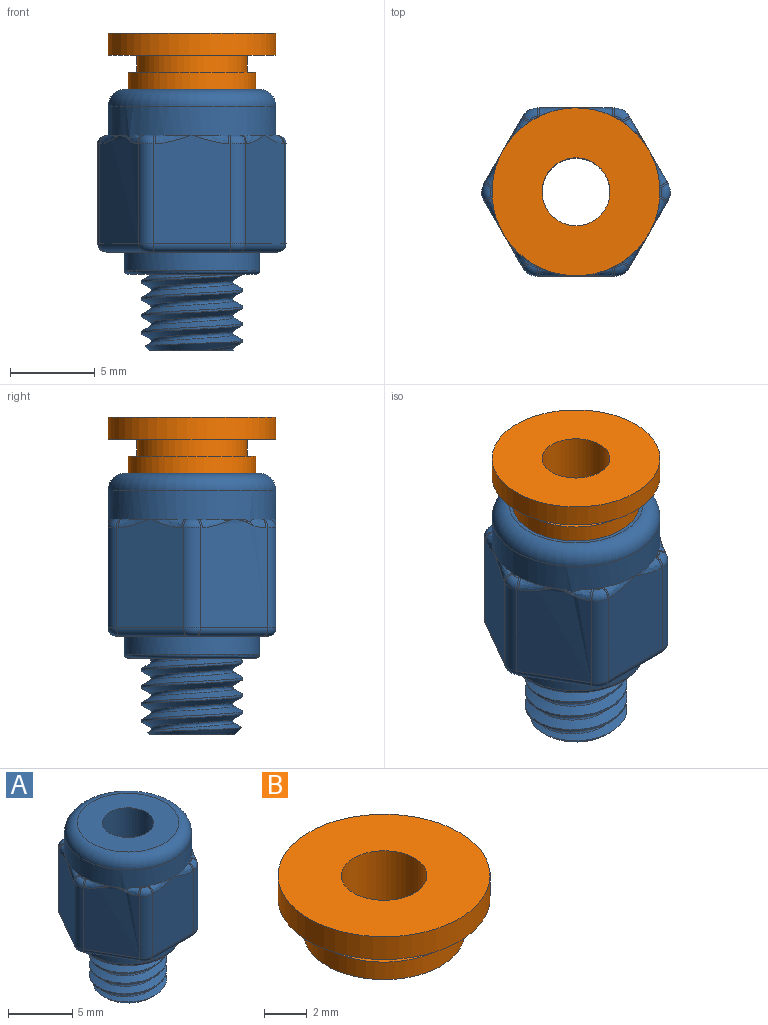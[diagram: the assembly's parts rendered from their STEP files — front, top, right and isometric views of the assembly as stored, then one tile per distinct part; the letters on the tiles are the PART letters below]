
ASSEMBLY  parts=2 mates=1
PART A: 76 faces, bbox 11.7x11.1x16.2 mm
  f0: plane 0.6x0.35mm, normal (0,0,1), area 0.1mm2, adj f1,f73,f74,f75
  f1: cylinder r=0.5mm len=0.5mm, axis (0.5,-0.87,0), area 0.1mm2, adj f0,f2,f72,f75
  f2: plane 6.78x4.33mm, normal (0.87,0.5,0), area 27.7mm2, adj f1,f3,f67,f68,f69,f70,f71,f72
  f3: cylinder r=0.5mm len=0.5mm, axis (0.5,-0.87,0), area 0.1mm2, adj f2,f4,f66,f68
  f4: plane 0.7x0.12mm, normal (0,0,1), area 0.1mm2, adj f3,f5,f66,f73
  f5: cylinder r=0.5mm len=0.5mm, axis (-0.5,-0.87,0), area 0.1mm2, adj f4,f6,f65,f66
  f6: plane 6.4x3.95mm, normal (0.87,-0.5,0), area 27.7mm2, adj f5,f7,f62,f63,f64,f65,f71
  f7: cylinder r=0.5mm len=0.5mm, axis (-0.5,-0.87,0), area 0.1mm2, adj f6,f8,f61,f62
  f8: torus R=0.5mm, axis (0,0,1), area 0.7mm2, adj f7,f9,f61,f64
  f9: cylinder r=0.5mm len=0.5mm, axis (-1,0,0), area 0.1mm2, adj f8,f10,f60,f61
  f10: plane 6.4x4.56mm, normal (0,-1,0), area 27.7mm2, adj f9,f11,f57,f58,f59,f60,f64
  f11: cylinder r=0.5mm len=4.56mm, axis (1,0,0), area 3.6mm2, adj f10,f12,f55,f56
  f12: plane 10.12x8.9mm, normal (0,0,-1), area 18.3mm2, adj f11,f13,f25,f49,f50,f51,f52,f53
  f13: cylinder r=4mm len=8mm, axis (0,0,1), area 26.4mm2, adj f12,f14
  f14: torus R=3.75mm, axis (0,0,-1), area 9.6mm2, adj f13,f15
  f15: plane 7.78x7.78mm, normal (0,0,-1), area 21.4mm2, adj f14,f16,f22,f23,f24
  f16: bspline ~6.93x6mm, area 45.7mm2, adj f15,f17,f21,f22,f24
  f17: plane 5.03x4.95mm, normal (0,0,-1), area 6.7mm2, adj f16,f18,f21,f22,f23
  f18: cylinder r=2mm len=15.4mm, axis (0,0,-1), area 193.5mm2, adj f17,f19
  f19: plane 7.9x7.9mm, normal (0,0,1), area 36.5mm2, adj f18,f20
  f20: torus R=3.95mm, axis (0,0,1), area 45.3mm2, adj f19,f73
  f21: cone r=2.5mm half-angle=45deg, axis (0,0,1), area 4.9mm2, adj f16,f17,f23,f24
  f22: bspline ~5.68x5.25mm, area 19.2mm2, adj f15,f16,f17,f23
  f23: bspline ~6.93x6mm, area 45.7mm2, adj f15,f17,f21,f22,f24
  f24: cylinder r=3mm len=6mm, axis (0,0,1), area 10.8mm2, adj f15,f16,f21,f23
  f25: cylinder r=0.5mm len=4.2mm, axis (-0.5,-0.87,0), area 3.6mm2, adj f12,f26,f49,f54
  f26: plane 6.4x3.95mm, normal (-0.87,0.5,0), area 27.7mm2, adj f25,f27,f34,f35,f36,f37,f48
  f27: cylinder r=1mm len=5.9mm, axis (0,0,-1), area 6.2mm2, adj f26,f28,f33,f54
  f28: plane 6.4x4.56mm, normal (0,1,0), area 27.7mm2, adj f27,f29,f30,f31,f53,f69,f74
  f29: bspline ~2.22x0.53mm, area 0.5mm2, adj f28,f73,f74
  f30: bspline ~2.22x0.53mm, area 0.5mm2, adj f28,f31,f73
  f31: cylinder r=0.5mm len=0.5mm, axis (1,0,0), area 0.1mm2, adj f28,f30,f32,f33
  f32: plane 0.6x0.35mm, normal (0,0,1), area 0.1mm2, adj f31,f33,f34,f73
  f33: torus R=0.5mm, axis (0,0,1), area 0.7mm2, adj f27,f31,f32,f34
  f34: cylinder r=0.5mm len=0.5mm, axis (0.5,0.87,0), area 0.1mm2, adj f26,f32,f33,f35
  f35: bspline ~2.02x1.64mm, area 0.5mm2, adj f26,f34,f73
  f36: bspline ~2.31x1.19mm, area 0.5mm2, adj f26,f37,f73
  f37: cylinder r=0.5mm len=0.5mm, axis (0.5,0.87,0), area 0.1mm2, adj f26,f36,f38,f47
  f38: plane 0.7x0.12mm, normal (0,0,1), area 0.1mm2, adj f37,f39,f47,f73
  f39: cylinder r=0.5mm len=0.5mm, axis (-0.5,0.87,0), area 0.1mm2, adj f38,f40,f46,f47
  f40: plane 6.78x4.33mm, normal (-0.87,-0.5,0), area 27.7mm2, adj f39,f41,f42,f45,f46,f48,f50,f57
  f41: bspline ~2.06x1.67mm, area 0.5mm2, adj f40,f42,f73
  f42: cylinder r=0.5mm len=0.5mm, axis (-0.5,0.87,0), area 0.1mm2, adj f40,f41,f43,f44
  f43: plane 0.6x0.35mm, normal (0,0,1), area 0.1mm2, adj f42,f44,f58,f73
  f44: torus R=0.5mm, axis (0,0,1), area 0.7mm2, adj f42,f43,f57,f58
  f45: bspline ~1.33x0.69mm, area 0.1mm2, adj f40,f73
  f46: bspline ~1.93x0.97mm, area 0.3mm2, adj f39,f40,f73
  f47: torus R=0.5mm, axis (0,0,1), area 0.7mm2, adj f37,f38,f39,f48
  f48: cylinder r=1mm len=5.9mm, axis (0,0,-1), area 6.2mm2, adj f26,f40,f47,f49
  f49: torus R=0.5mm, axis (0,0,1), area 0.7mm2, adj f12,f25,f48,f50
  f50: cylinder r=0.5mm len=4.2mm, axis (0.5,-0.87,0), area 3.6mm2, adj f12,f40,f49,f55
  f51: torus R=0.5mm, axis (0,0,1), area 0.7mm2, adj f12,f63,f70,f71
  f52: torus R=0.5mm, axis (0,0,1), area 0.7mm2, adj f12,f53,f69,f70
  f53: cylinder r=0.5mm len=4.56mm, axis (-1,0,0), area 3.6mm2, adj f12,f28,f52,f54
  f54: torus R=0.5mm, axis (0,0,1), area 0.7mm2, adj f12,f25,f27,f53
  f55: torus R=0.5mm, axis (0,0,1), area 0.7mm2, adj f11,f12,f50,f57
  f56: torus R=0.5mm, axis (0,0,1), area 0.7mm2, adj f11,f12,f63,f64
  f57: cylinder r=1mm len=5.9mm, axis (0,0,-1), area 6.2mm2, adj f10,f40,f44,f55
  f58: cylinder r=0.5mm len=0.5mm, axis (-1,0,0), area 0.1mm2, adj f10,f43,f44,f59
  f59: bspline ~2.22x0.53mm, area 0.5mm2, adj f10,f58,f73
  f60: bspline ~2.22x0.53mm, area 0.5mm2, adj f9,f10,f73
  f61: plane 0.6x0.35mm, normal (0,0,1), area 0.1mm2, adj f7,f8,f9,f73
  f62: bspline ~2.02x1.64mm, area 0.5mm2, adj f6,f7,f73
  f63: cylinder r=0.5mm len=4.2mm, axis (0.5,0.87,0), area 3.6mm2, adj f6,f12,f51,f56
  f64: cylinder r=1mm len=5.9mm, axis (0,0,-1), area 6.2mm2, adj f6,f8,f10,f56
  f65: bspline ~2.31x1.19mm, area 0.5mm2, adj f5,f6,f73
  f66: torus R=0.5mm, axis (0,0,1), area 0.7mm2, adj f3,f4,f5,f71
  f67: bspline ~1.33x0.69mm, area 0.1mm2, adj f2,f73
  f68: bspline ~1.93x0.97mm, area 0.3mm2, adj f2,f3,f73
  f69: cylinder r=1mm len=5.9mm, axis (0,0,-1), area 6.2mm2, adj f2,f28,f52,f75
  f70: cylinder r=0.5mm len=4.2mm, axis (-0.5,0.87,0), area 3.6mm2, adj f2,f12,f51,f52
  f71: cylinder r=1mm len=5.9mm, axis (0,0,-1), area 6.2mm2, adj f2,f6,f51,f66
  f72: bspline ~2.06x1.67mm, area 0.5mm2, adj f1,f2,f73
  f73: cylinder r=4.95mm len=9.9mm, axis (0,0,-1), area 52.9mm2, adj f0,f4,f20,f29,f30,f32,f35,f36
  f74: cylinder r=0.5mm len=0.5mm, axis (1,0,0), area 0.1mm2, adj f0,f28,f29,f75
  f75: torus R=0.5mm, axis (0,0,1), area 0.7mm2, adj f0,f1,f69,f74
PART B: 8 faces, bbox 9.9x9.9x3.3 mm
  f0: cylinder r=3.75mm len=7.5mm, axis (0,0,-1), area 23.6mm2, adj f1,f2
  f1: plane 7.5x7.5mm, normal (0,0,1), area 11mm2, adj f0,f3
  f2: plane 7.5x7.5mm, normal (0,0,-1), area 31.6mm2, adj f0,f7
  f3: cylinder r=3.25mm len=6.5mm, axis (0,0,-1), area 20.4mm2, adj f1,f6
  f4: cylinder r=4.95mm len=9.9mm, axis (0,0,-1), area 40.4mm2, adj f5,f6
  f5: plane 9.9x9.9mm, normal (0,0,1), area 64.4mm2, adj f4,f7
  f6: plane 9.9x9.9mm, normal (0,0,-1), area 43.8mm2, adj f3,f4
  f7: cylinder r=2mm len=4mm, axis (0,0,1), area 41.5mm2, adj f2,f5
PLACE A at identity fixed
PLACE B at identity
MATE fastened B.f0 <-> A.f13  axis (0,0,-1) through (0,0,9.6)mm
